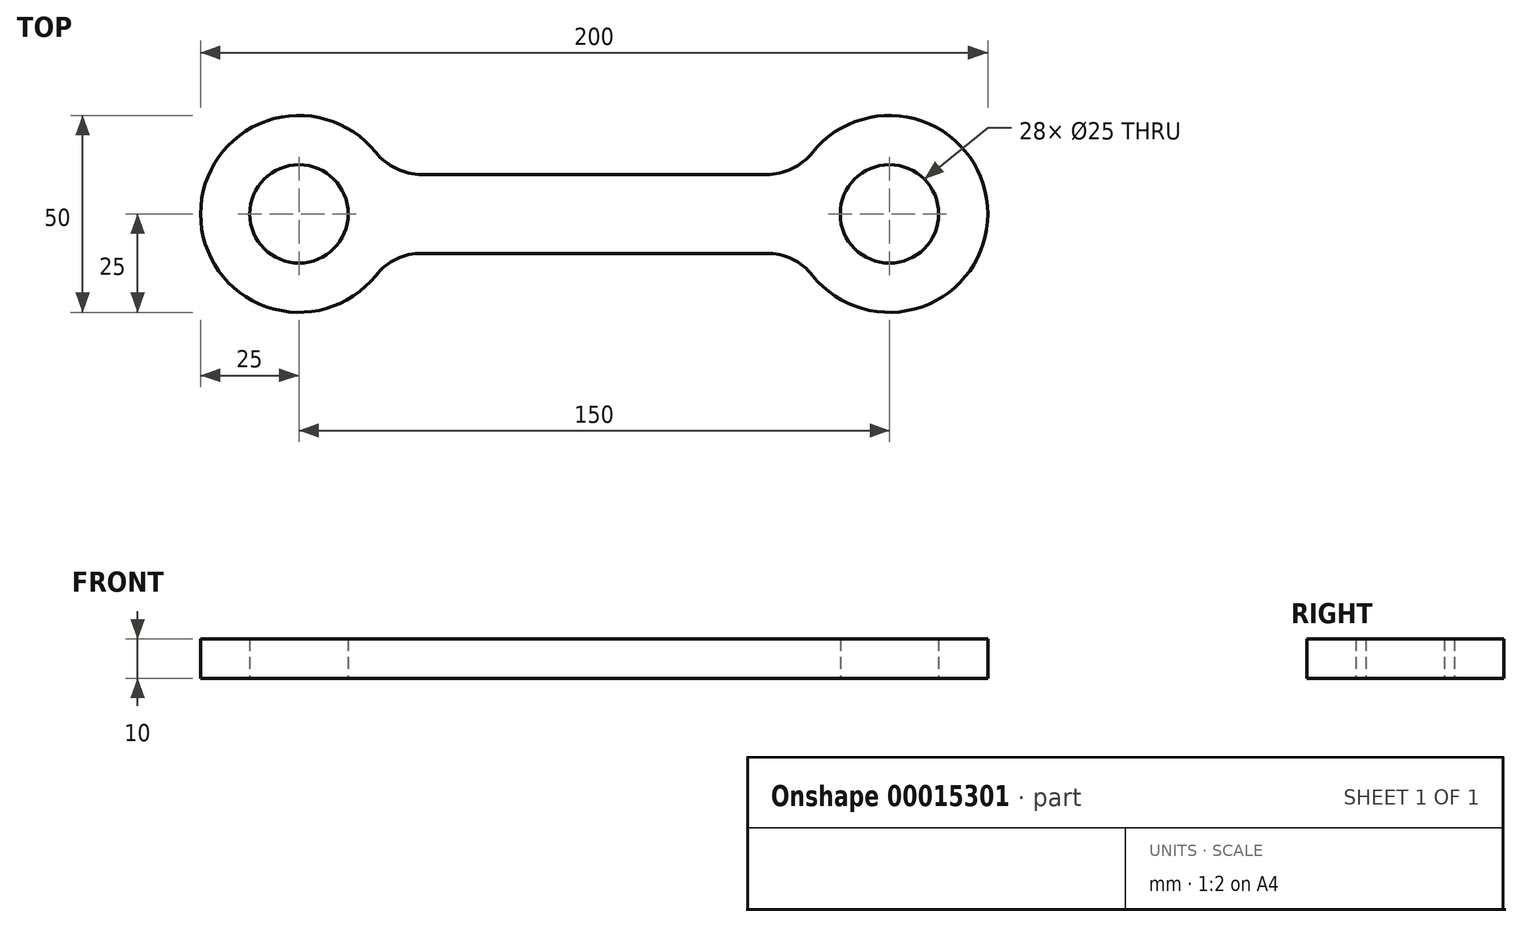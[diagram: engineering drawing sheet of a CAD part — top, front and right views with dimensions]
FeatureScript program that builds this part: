
annotation { "Feature Type Name" : "Feature", "Feature Type Description" : "" }
export const myFeature = defineFeature(function(context is Context, id is Id, definition is map)
    precondition{}
    {
        {
            var Q0;
            Q0=qCreatedBy(makeId("Top.planeOp"),FACE);
            var sketch = newSketch(context, id + "F0", { "sketchPlane" : qUnion([Q0])});
            skArc(sketch, "E0", {"start": v(19.52, 15.63) * mm, "mid": v(-25, 0) * mm, "end": v(19.52, -15.63) * mm});
            skArc(sketch, "E1", {"start": v(130.48, -15.62) * mm, "mid": v(175, 0) * mm, "end": v(130.48, 15.63) * mm});
            skLineSegment(sketch, "E2", {"start": v(31.22, 10) * mm, "end": v(118.78, 10) * mm});
            skLineSegment(sketch, "E3", {"start": v(0, 0) * mm, "end": v(150, 0) * mm, "construction": true});
            skLineSegment(sketch, "E4.MirrorCS", {"start": v(31.22, -10) * mm, "end": v(118.78, -10) * mm});
            skPoint(sketch, "E5.visualSharp", {"position": v(22.91, 10) * mm});
            skArc(sketch, "E5.filletArc", {"start": v(19.52, 15.62) * mm, "mid": v(24.73, 11.48) * mm, "end": v(31.22, 10) * mm});
            skPoint(sketch, "E6.visualSharp", {"position": v(22.91, -10) * mm});
            skArc(sketch, "E6.filletArc", {"start": v(31.22, -10) * mm, "mid": v(24.73, -11.48) * mm, "end": v(19.52, -15.62) * mm});
            skPoint(sketch, "E7.visualSharp", {"position": v(127.09, -10) * mm});
            skArc(sketch, "E7.filletArc", {"start": v(130.48, -15.62) * mm, "mid": v(125.27, -11.48) * mm, "end": v(118.78, -10) * mm});
            skPoint(sketch, "E8.visualSharp", {"position": v(127.09, 10) * mm});
            skArc(sketch, "E8.filletArc", {"start": v(118.78, 10) * mm, "mid": v(125.27, 11.48) * mm, "end": v(130.48, 15.62) * mm});
            skCircle(sketch, "E9", {"center": v(0, 0) * mm, "radius": 12.5 * mm});
            skCircle(sketch, "E10", {"center": v(150, 0) * mm, "radius": 12.5 * mm});
            skSolve(sketch);
        }
        {
            var Q0;
            Q0=qSketchRegion(id+"F0",true);
            extrude(context, id + "F1", {"entities" : qUnion([Q0]), "depth" : 10 * mm});
        }
    });
